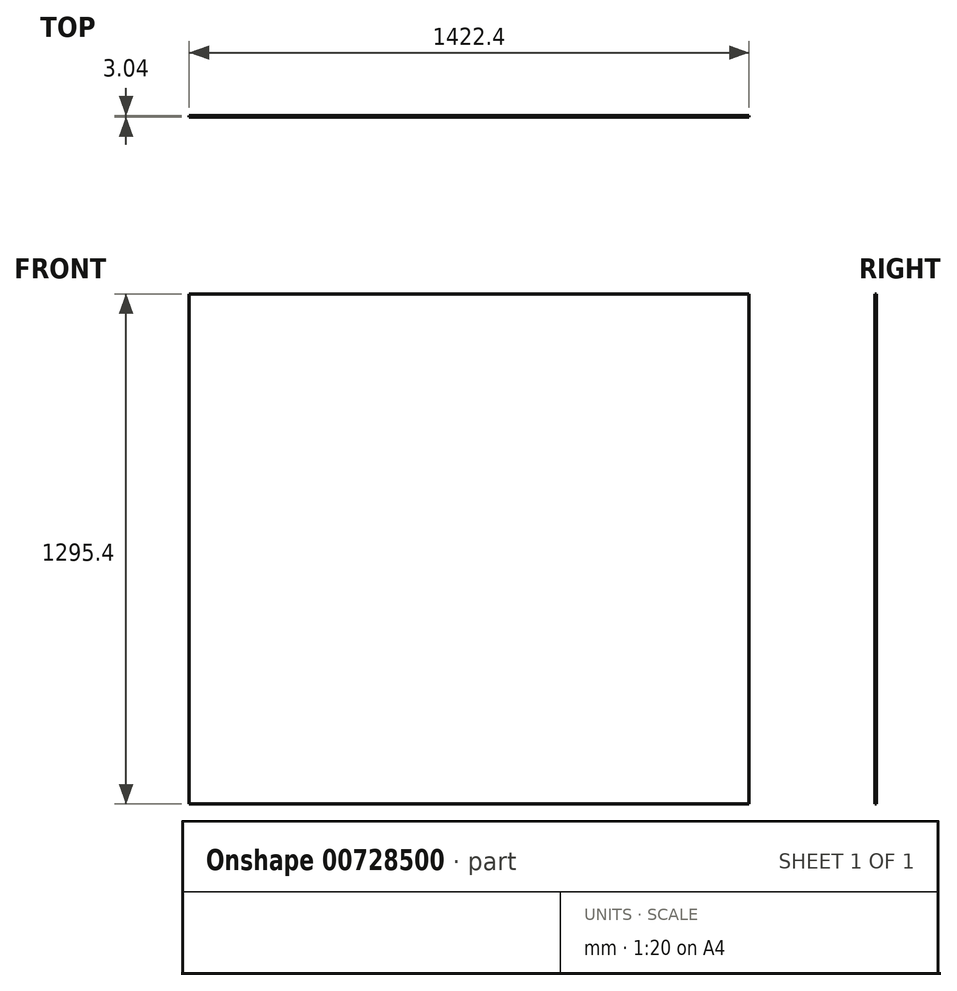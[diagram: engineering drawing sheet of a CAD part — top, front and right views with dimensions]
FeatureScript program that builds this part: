
annotation { "Feature Type Name" : "Feature", "Feature Type Description" : "" }
export const myFeature = defineFeature(function(context is Context, id is Id, definition is map)
    precondition{}
    {
        {
            var Q0;
            Q0=qCreatedBy(makeId("Front.planeOp"),FACE);
            var sketch = newSketch(context, id + "F0", { "sketchPlane" : qUnion([Q0])});
            skLineSegment(sketch, "E0.bottom", {"start": v(-711.2, 647.7) * mm, "end": v(711.2, 647.7) * mm});
            skLineSegment(sketch, "E0.top", {"start": v(-711.2, -647.7) * mm, "end": v(711.2, -647.7) * mm});
            skLineSegment(sketch, "E0.left", {"start": v(-711.2, 647.7) * mm, "end": v(-711.2, -647.7) * mm});
            skLineSegment(sketch, "E0.right", {"start": v(711.2, 647.7) * mm, "end": v(711.2, -647.7) * mm});
            skPoint(sketch, "E0.middle", {"position": v(0, 0) * mm});
            skSolve(sketch);
        }
        {
            var Q0;
            Q0=makeQuery(id+"F0.imprint","IMPRINT",FACE,{"disambiguationData":[TD([[makeQuery(id+"F0.imprint","IMPRINT",EDGE,{"derivedFrom":sQuery(id+"F0.wireOp",EDGE,"E0.bottom")}),-1.0]])]});
            extrude(context, id + "F1", {"entities" : qUnion([Q0]), "endBound" : BoundingType.SYMMETRIC, "depth" : 3.05 * mm, "offsetDistance" : 25.4 * mm});
        }
    });
